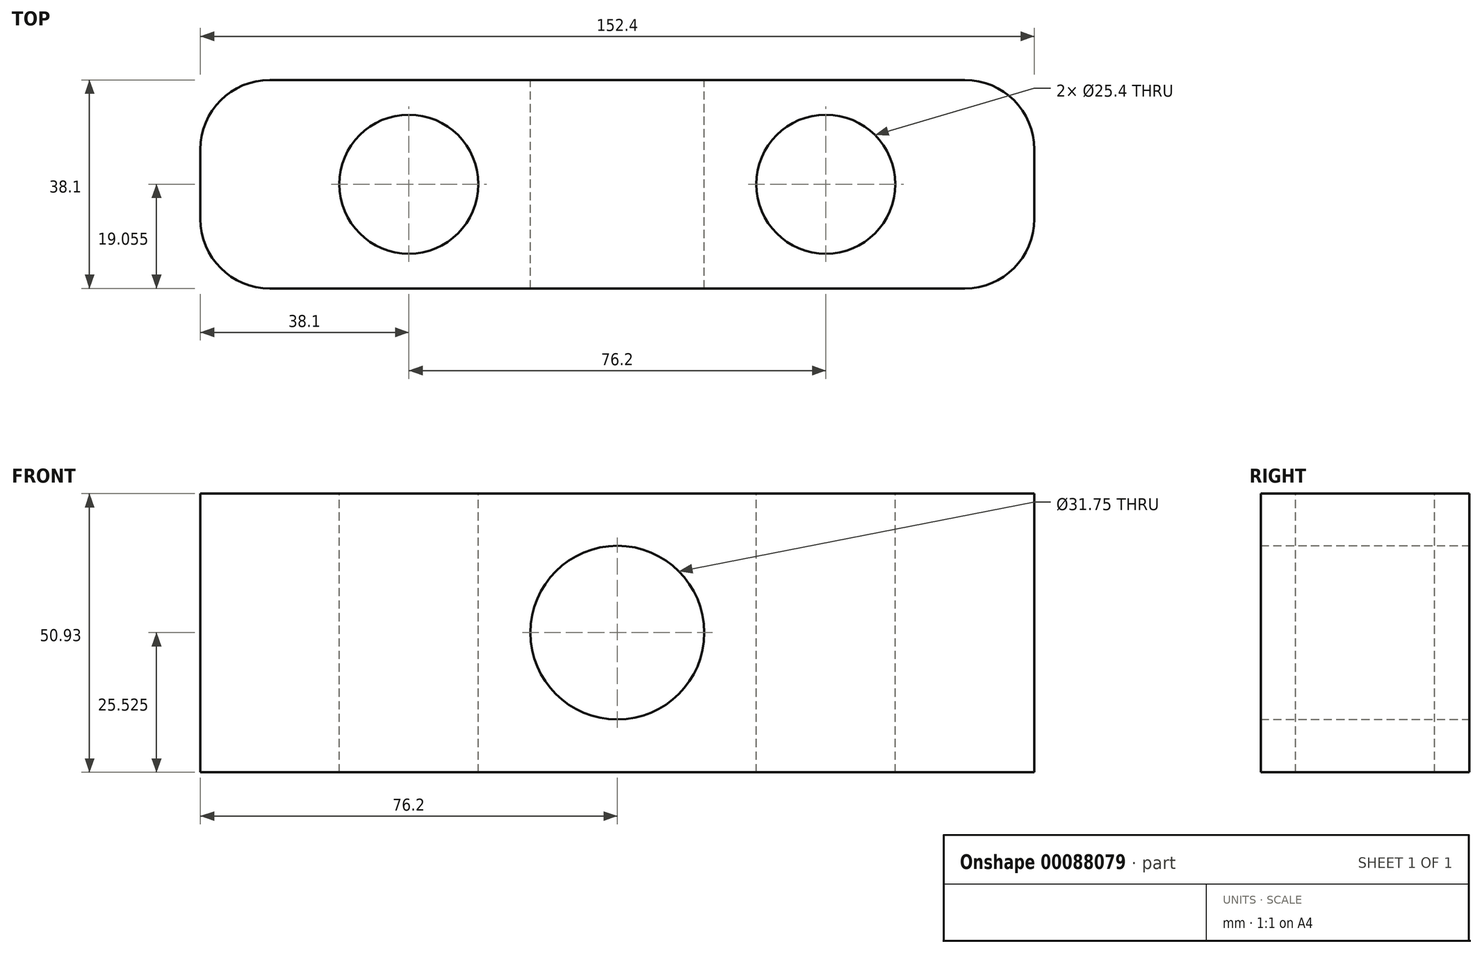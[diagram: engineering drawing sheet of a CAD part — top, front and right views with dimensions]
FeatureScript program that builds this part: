
annotation { "Feature Type Name" : "Feature", "Feature Type Description" : "" }
export const myFeature = defineFeature(function(context is Context, id is Id, definition is map)
    precondition{}
    {
        {
            var Q0;
            Q0=qCreatedBy(makeId("Top.planeOp"),FACE);
            var sketch = newSketch(context, id + "F0", { "sketchPlane" : qUnion([Q0])});
            skCircle(sketch, "E0", {"center": v(0, 0) * mm, "radius": 15.88 * mm});
            skCircle(sketch, "E1", {"center": v(0, 0) * mm, "radius": 25.4 * mm, "construction": true});
            skLineSegment(sketch, "E2.bottom", {"start": v(0, 25.4) * mm, "end": v(76.2, 25.4) * mm});
            skLineSegment(sketch, "E2.top", {"start": v(0, -25.53) * mm, "end": v(76.2, -25.53) * mm});
            skLineSegment(sketch, "E2.left", {"start": v(0, 25.4) * mm, "end": v(0, -25.53) * mm});
            skLineSegment(sketch, "E2.right", {"start": v(76.2, 25.4) * mm, "end": v(76.2, -25.53) * mm});
            skLineSegment(sketch, "E3.bottom", {"start": v(0, 25.4) * mm, "end": v(-76.2, 25.4) * mm});
            skLineSegment(sketch, "E3.top", {"start": v(0, -25.53) * mm, "end": v(-76.2, -25.53) * mm});
            skLineSegment(sketch, "E3.right", {"start": v(-76.2, 25.4) * mm, "end": v(-76.2, -25.53) * mm});
            skSolve(sketch);
        }
        {
            var Q0;
            {var subQ1=sQuery(id+"F0.wireOp",EDGE,"E2.bottom");Q0=makeQuery(id+"F0.imprint","IMPRINT",FACE,{"disambiguationData":[TD([[makeQuery(id+"F0.imprint","IMPRINT",EDGE,{"derivedFrom":subQ1}),-1.0]])]});}
            var Q1;
            {var subQ1=sQuery(id+"F0.wireOp",EDGE,"E3.bottom");Q1=makeQuery(id+"F0.imprint","IMPRINT",FACE,{"disambiguationData":[TD([[makeQuery(id+"F0.imprint","IMPRINT",EDGE,{"derivedFrom":subQ1}),1.0]])]});}
            extrude(context, id + "F1", {"entities" : qUnion([Q0, Q1]), "depth" : 38.1 * mm});
        }
        {
            var Q0;
            Q0=makeQuery(id+"F1.opExtrude","SWEPT_FACE",FACE,{"disambiguationData":[OSD([sQuery(id+"F0.wireOp",EDGE,"E2.bottom"),sQuery(id+"F0.wireOp",EDGE,"E3.bottom")])]});
            var sketch = newSketch(context, id + "F2", { "sketchPlane" : qUnion([Q0])});
            skLineSegment(sketch, "E4", {"start": v(-76.2, 19.05) * mm, "end": v(76.2, 19.05) * mm, "construction": true});
            skLineSegment(sketch, "E5", {"start": v(0, 38.1) * mm, "end": v(0, 0) * mm, "construction": true});
            skLineSegment(sketch, "E6", {"start": v(0, 0) * mm, "end": v(-76.2, 38.1) * mm, "construction": true});
            skLineSegment(sketch, "E7", {"start": v(-76.2, 38.1) * mm, "end": v(-76.2, 0) * mm, "construction": true});
            skLineSegment(sketch, "E8", {"start": v(-76.2, 0) * mm, "end": v(0, 38.1) * mm, "construction": true});
            skLineSegment(sketch, "E9", {"start": v(0, 38.1) * mm, "end": v(76.2, 0) * mm, "construction": true});
            skLineSegment(sketch, "E10", {"start": v(76.2, 0) * mm, "end": v(76.2, 38.1) * mm, "construction": true});
            skLineSegment(sketch, "E11", {"start": v(76.2, 38.1) * mm, "end": v(0, 0) * mm, "construction": true});
            skCircle(sketch, "E12", {"center": v(-38.1, 19.05) * mm, "radius": 12.7 * mm});
            skCircle(sketch, "E13", {"center": v(38.1, 19.05) * mm, "radius": 12.7 * mm});
            skSolve(sketch);
        }
        {
            var Q0;
            Q0=makeQuery(id+"F2.imprint","IMPRINT",FACE,{"disambiguationData":[TD([[makeQuery(id+"F2.imprint","IMPRINT",EDGE,{"derivedFrom":sQuery(id+"F2.wireOp",EDGE,"E12")}),1.0]])]});
            var Q1;
            Q1=makeQuery(id+"F2.imprint","IMPRINT",FACE,{"disambiguationData":[TD([[makeQuery(id+"F2.imprint","IMPRINT",EDGE,{"derivedFrom":sQuery(id+"F2.wireOp",EDGE,"E13")}),1.0]])]});
            var Q2;
            Q2=sQuery(id+"F2.wireOp",EDGE,"E12");
            var Q3;
            Q3=sQuery(id+"F2.wireOp",EDGE,"E13");
            extrude(context, id + "F3", {"entities" : qUnion([Q0, Q1]), "operationType" : NewBodyOperationType.REMOVE, "surfaceEntities" : qUnion([Q2, Q3]), "endBound" : BoundingType.THROUGH_ALL, "oppositeDirection" : true, "depth" : 25.4 * mm});
        }
        {
            var Q0;
            Q0=makeQuery(id+"F1.opExtrude","SWEPT_BODY",BODY,{"disambiguationData":[OSD([sQuery(id+"F0.wireOp",EDGE,"E0"),sQuery(id+"F0.wireOp",EDGE,"E2.bottom"),sQuery(id+"F0.wireOp",EDGE,"E2.top"),sQuery(id+"F0.wireOp",EDGE,"E2.right"),sQuery(id+"F0.wireOp",EDGE,"E3.bottom"),sQuery(id+"F0.wireOp",EDGE,"E3.top"),sQuery(id+"F0.wireOp",EDGE,"E3.right")])]});
            var Q1;
            Q1=makeQuery(id+"F1.opExtrude","CAP_EDGE",EDGE,{"disambiguationData":[OSD([sQuery(id+"F0.wireOp",EDGE,"E2.top"),sQuery(id+"F0.wireOp",EDGE,"E3.top")])],"isStart":false});
            transform(context, id + "F4", {"entities" : qUnion([Q0]), "transformType" : TransformType.ROTATION, "transformAxis" : qUnion([Q1]), "angle" : 90 * degree, "makeCopy" : false});
        }
        {
            var Q0;
            Q0=makeQuery(id+"F1.opExtrude","CAP_EDGE",EDGE,{"disambiguationData":[OSD([sQuery(id+"F0.wireOp",EDGE,"E2.right")])],"isStart":false});
            var Q1;
            Q1=makeQuery(id+"F1.opExtrude","CAP_EDGE",EDGE,{"disambiguationData":[OSD([sQuery(id+"F0.wireOp",EDGE,"E2.right")])],"isStart":true});
            var Q2;
            Q2=makeQuery(id+"F1.opExtrude","CAP_EDGE",EDGE,{"disambiguationData":[OSD([sQuery(id+"F0.wireOp",EDGE,"E3.right")])],"isStart":false});
            var Q3;
            Q3=makeQuery(id+"F1.opExtrude","CAP_EDGE",EDGE,{"disambiguationData":[OSD([sQuery(id+"F0.wireOp",EDGE,"E3.right")])],"isStart":true});
            fillet(context, id + "F5", {"entities" : qUnion([Q0, Q1, Q2, Q3]), "radius" : 12.7 * mm, "tangentPropagation" : true, "allowEdgeOverflow" : false});
        }
        {
            var Q0;
            Q0=makeQuery(id+"F1.opExtrude","SWEPT_BODY",BODY,{"disambiguationData":[OSD([sQuery(id+"F0.wireOp",EDGE,"E0"),sQuery(id+"F0.wireOp",EDGE,"E2.bottom"),sQuery(id+"F0.wireOp",EDGE,"E2.top"),sQuery(id+"F0.wireOp",EDGE,"E2.right"),sQuery(id+"F0.wireOp",EDGE,"E3.bottom"),sQuery(id+"F0.wireOp",EDGE,"E3.top"),sQuery(id+"F0.wireOp",EDGE,"E3.right")])]});
            transform(context, id + "F6", {"entities" : qUnion([Q0]), "transformType" : TransformType.TRANSLATION_3D, "dx" : 0 * mm, "dy" : 0 * mm, "dz" : 70.31 * mm, "makeCopy" : true});
        }
        {
            var Q0;
            Q0=makeQuery(id+"F6.opPattern","COPY",BODY,{"derivedFrom":makeQuery(id+"F1.opExtrude","SWEPT_BODY",BODY,{"disambiguationData":[OSD([sQuery(id+"F0.wireOp",EDGE,"E0"),sQuery(id+"F0.wireOp",EDGE,"E2.bottom"),sQuery(id+"F0.wireOp",EDGE,"E2.top"),sQuery(id+"F0.wireOp",EDGE,"E2.right"),sQuery(id+"F0.wireOp",EDGE,"E3.bottom"),sQuery(id+"F0.wireOp",EDGE,"E3.top"),sQuery(id+"F0.wireOp",EDGE,"E3.right")])]}),"instanceName":"1"});
            deleteBodies(context, id + "F7", {"entities" : qUnion([Q0])});
        }
    });
